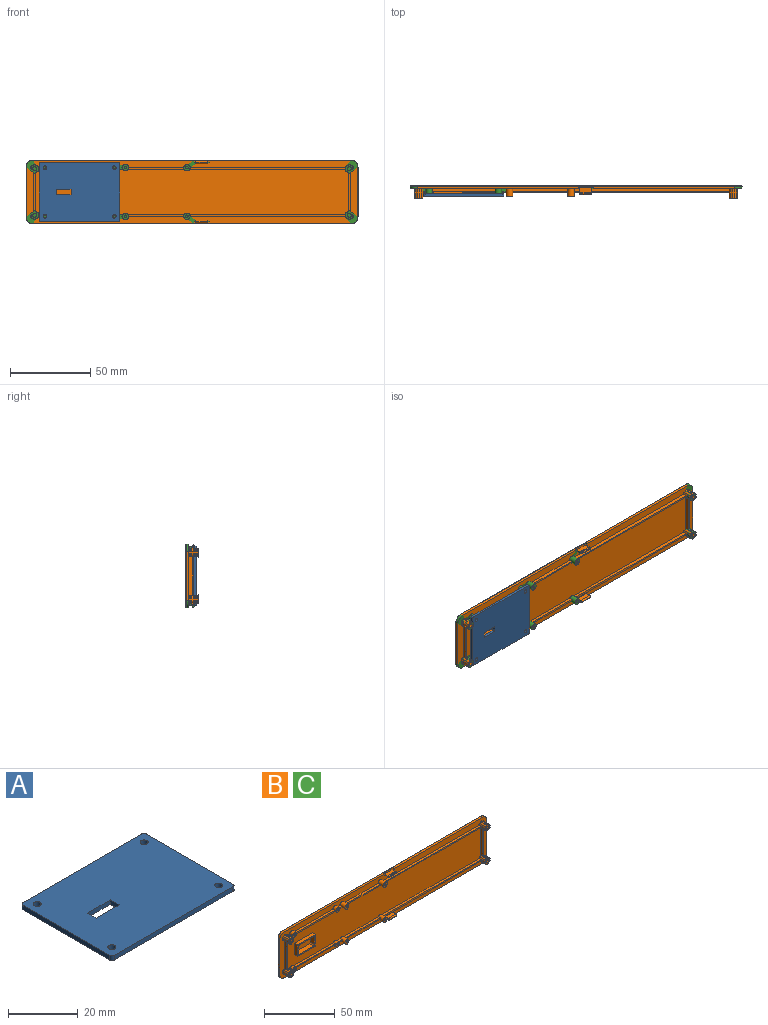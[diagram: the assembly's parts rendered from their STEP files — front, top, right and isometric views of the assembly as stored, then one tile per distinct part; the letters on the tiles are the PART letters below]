
ASSEMBLY  parts=3 mates=1
PART A: 18 faces, bbox 50x37x1.6 mm
  f0: cylinder r=1mm len=1.6mm, axis (0,0,-1), area 2.5mm2, adj f1,f15,f16,f17
  f1: plane 48x1.6mm, normal (0,-1,0), area 76.8mm2, adj f0,f2,f16,f17
  f2: cylinder r=1mm len=1.6mm, axis (0,0,-1), area 2.5mm2, adj f1,f3,f16,f17
  f3: plane 35x1.6mm, normal (1,0,0), area 56mm2, adj f2,f4,f16,f17
  f4: cylinder r=1mm len=1.6mm, axis (0,0,-1), area 2.5mm2, adj f3,f5,f16,f17
  f5: plane 48x1.6mm, normal (0,1,0), area 76.8mm2, adj f4,f6,f16,f17
  f6: cylinder r=1mm len=1.6mm, axis (0,0,-1), area 2.5mm2, adj f5,f15,f16,f17
  f7: plane 3.56x1.6mm, normal (-1,0,0), area 5.7mm2, adj f8,f14,f16,f17
  f8: plane 9.31x1.6mm, normal (0,1,0), area 14.9mm2, adj f7,f9,f16,f17
  f9: plane 3.56x1.6mm, normal (1,0,0), area 5.7mm2, adj f8,f14,f16,f17
  f10: cylinder r=1.15mm len=2.3mm, axis (0,0,-1), area 11.6mm2, adj f16,f17
  f11: cylinder r=1.15mm len=2.3mm, axis (0,0,-1), area 11.6mm2, adj f16,f17
  f12: cylinder r=1.15mm len=2.3mm, axis (0,0,-1), area 11.6mm2, adj f16,f17
  f13: cylinder r=1.15mm len=2.3mm, axis (0,0,-1), area 11.6mm2, adj f16,f17
  f14: plane 9.31x1.6mm, normal (0,-1,0), area 14.9mm2, adj f7,f9,f16,f17
  f15: plane 35x1.6mm, normal (-1,0,0), area 56mm2, adj f0,f6,f16,f17
  f16: plane 50x37mm, normal (0,0,1), area 1799.4mm2, adj f0,f1,f2,f3,f4,f5,f6,f7
  f17: plane 50x37mm, normal (0,0,-1), area 1799.4mm2, adj f0,f1,f2,f3,f4,f5,f6,f7
PART B: 227 faces, bbox 207.5x8x40.5 mm
  f0: cylinder r=0.3mm len=198mm, axis (-1,0,0), area 94.9mm2, adj f32,f36,f221,f222
  f1: cylinder r=0.3mm len=31mm, axis (0,0,-1), area 14.9mm2, adj f33,f36,f220,f222
  f2: cylinder r=0.3mm len=31mm, axis (0,0,1), area 14.9mm2, adj f34,f36,f219,f221
  f3: cylinder r=0.3mm len=198mm, axis (1,0,0), area 94.9mm2, adj f35,f36,f219,f220
  f4: cylinder r=1.25mm len=6mm, axis (0,-1,0), area 47.1mm2, adj f131,f150
  f5: cylinder r=2.7mm len=4mm, axis (0,-1,0), area 4mm2, adj f108,f110,f131,f204
  f6: cylinder r=1.25mm len=6mm, axis (0,-1,0), area 47.1mm2, adj f106,f127
  f7: cylinder r=2.7mm len=6mm, axis (0,-1,0), area 6mm2, adj f29,f106,f120,f121
  f8: cylinder r=1.25mm len=6mm, axis (0,-1,0), area 47.1mm2, adj f84,f102
  f9: cylinder r=2.7mm len=6mm, axis (0,-1,0), area 6mm2, adj f29,f84,f95,f96
  f10: cylinder r=1.25mm len=6mm, axis (0,-1,0), area 47.1mm2, adj f60,f80
  f11: cylinder r=2.7mm len=4mm, axis (0,-1,0), area 4mm2, adj f60,f73,f74,f200
  f12: cylinder r=0.8mm len=5mm, axis (0,-1,0), area 25.1mm2, adj f55,f56
  f13: cylinder r=0.8mm len=5mm, axis (0,-1,0), area 25.1mm2, adj f53,f54
  f14: cylinder r=0.8mm len=5mm, axis (0,-1,0), area 25.1mm2, adj f51,f52
  f15: cylinder r=0.8mm len=5mm, axis (0,-1,0), area 25.1mm2, adj f49,f50
  f16: cylinder r=2mm len=5mm, axis (0,-1,0), area 58.5mm2, adj f28,f29,f49,f211,f212,f213,f214,f215
  f17: cylinder r=0.8mm len=3mm, axis (0,1,0), area 15.1mm2, adj f47,f48
  f18: cylinder r=2mm len=4mm, axis (0,1,0), area 33.4mm2, adj f28,f29,f47,f208,f209,f210,f211,f212
  f19: cylinder r=0.8mm len=3mm, axis (0,1,0), area 15.1mm2, adj f45,f46
  f20: cylinder r=0.8mm len=3mm, axis (0,1,0), area 15.1mm2, adj f43,f44
  f21: cylinder r=0.8mm len=3mm, axis (0,1,0), area 15.1mm2, adj f41,f42
  f22: cylinder r=2mm len=4mm, axis (0,1,0), area 33.4mm2, adj f28,f29,f41,f205,f206,f207,f208,f209
  f23: cylinder r=2mm len=4mm, axis (0,1,0), area 33.4mm2, adj f28,f29,f43,f185,f186,f187,f188,f189
  f24: cylinder r=2mm len=5mm, axis (0,-1,0), area 58.6mm2, adj f28,f29,f53,f191,f192,f193,f194,f195
  f25: cylinder r=2mm len=4mm, axis (0,1,0), area 33.4mm2, adj f28,f29,f45,f188,f189,f190,f191,f192
  f26: cylinder r=2mm len=5mm, axis (0,-1,0), area 58.6mm2, adj f28,f29,f55,f194,f195,f196,f197,f198
  f27: cylinder r=2mm len=5mm, axis (0,-1,0), area 58.5mm2, adj f28,f29,f51,f201,f202,f203,f214,f215
  f28: plane 195x28mm, normal (0,-1,0), area 5253.7mm2, adj f16,f18,f22,f23,f24,f25,f26,f27
  f29: plane 206.7x39.7mm, normal (0,-1,0), area 2140.7mm2, adj f7,f9,f16,f18,f22,f23,f24,f25
  f30: cylinder r=2.3mm len=6mm, axis (0,-1,0), area 6.4mm2, adj f28,f29,f60,f68,f69,f201,f202,f203
  f31: cylinder r=2.3mm len=6mm, axis (0,-1,0), area 6.4mm2, adj f28,f29,f84,f90,f91,f197,f198,f199
  f32: plane 198x1.69mm, normal (0,-0.03,1), area 325.8mm2, adj f0,f29,f38,f40,f160,f161,f162
  f33: plane 31x1.69mm, normal (-1,-0.03,0), area 52.5mm2, adj f1,f29,f39,f40
  f34: plane 31x1.69mm, normal (1,-0.03,0), area 52.5mm2, adj f2,f29,f37,f38
  f35: plane 198x1.69mm, normal (0,-0.03,-1), area 325.8mm2, adj f3,f29,f37,f39,f172,f173,f174
  f36: plane 206.18x39.18mm, normal (0,1,0), area 8064.8mm2, adj f0,f1,f2,f3,f219,f220,f221,f222
  f37: cone r=4.4mm half-angle=1.5deg, axis (0,1,0), area 11.6mm2, adj f29,f34,f35,f219
  f38: cone r=4.4mm half-angle=1.5deg, axis (0,1,0), area 11.6mm2, adj f29,f32,f34,f221
  f39: cone r=4.4mm half-angle=1.5deg, axis (0,1,0), area 11.6mm2, adj f29,f33,f35,f220
  f40: cone r=4.4mm half-angle=1.5deg, axis (0,1,0), area 11.6mm2, adj f29,f32,f33,f222
  f41: plane 4x4mm, normal (0,-1,0), area 10.6mm2, adj f21,f22
  f42: plane 1.6x1.6mm, normal (0,-1,0), area 2mm2, adj f21
  f43: plane 4x4mm, normal (0,-1,0), area 10.6mm2, adj f20,f23
  f44: plane 1.6x1.6mm, normal (0,-1,0), area 2mm2, adj f20
  f45: plane 4x4mm, normal (0,-1,0), area 10.6mm2, adj f19,f25
  f46: plane 1.6x1.6mm, normal (0,-1,0), area 2mm2, adj f19
  f47: plane 4x4mm, normal (0,-1,0), area 10.6mm2, adj f17,f18
  f48: plane 1.6x1.6mm, normal (0,-1,0), area 2mm2, adj f17
  f49: plane 4x4mm, normal (0,-1,0), area 10.6mm2, adj f15,f16
  f50: plane 1.6x1.6mm, normal (0,-1,0), area 2mm2, adj f15
  f51: plane 4x4mm, normal (0,-1,0), area 10.6mm2, adj f14,f27
  f52: plane 1.6x1.6mm, normal (0,-1,0), area 2mm2, adj f14
  f53: plane 4x4mm, normal (0,-1,0), area 10.6mm2, adj f13,f24
  f54: plane 1.6x1.6mm, normal (0,-1,0), area 2mm2, adj f13
  f55: plane 4x4mm, normal (0,-1,0), area 10.6mm2, adj f12,f26
  f56: plane 1.6x1.6mm, normal (0,-1,0), area 2mm2, adj f12
  f57: cylinder r=2.7mm len=6mm, axis (0,-1,0), area 6mm2, adj f29,f58,f59,f60
  f58: plane 6x0.35mm, normal (0.5,0,-0.87), area 2.4mm2, adj f29,f57,f60,f79
  f59: plane 6x0.35mm, normal (-0.5,0,0.87), area 2.4mm2, adj f29,f57,f60,f61
  f60: plane 5.4x5.1mm, normal (0,-1,0), area 14.1mm2, adj f10,f11,f30,f57,f58,f59,f61,f62
  f61: cylinder r=2.3mm len=6mm, axis (0,-1,0), area 8.4mm2, adj f29,f59,f60,f62
  f62: plane 6x0.41mm, normal (1,0,0), area 2.4mm2, adj f29,f60,f61,f63
  f63: cylinder r=2.7mm len=6mm, axis (0,-1,0), area 6mm2, adj f29,f60,f62,f64
  f64: plane 6x0.41mm, normal (-1,0,0), area 2.4mm2, adj f29,f60,f63,f65
  f65: cylinder r=2.3mm len=6mm, axis (0,-1,0), area 8.4mm2, adj f29,f60,f64,f66
  f66: plane 6x0.35mm, normal (0.5,0,0.87), area 2.4mm2, adj f29,f60,f65,f67
  f67: cylinder r=2.7mm len=6mm, axis (0,-1,0), area 6mm2, adj f29,f60,f66,f68
  f68: plane 6x0.35mm, normal (-0.5,0,-0.87), area 2.4mm2, adj f29,f30,f60,f67
  f69: plane 6x0.35mm, normal (-0.5,0,0.87), area 2.4mm2, adj f28,f30,f60,f70
  f70: cylinder r=2.7mm len=6mm, axis (0,-1,0), area 6mm2, adj f28,f60,f69,f71
  f71: plane 6x0.35mm, normal (0.5,0,-0.87), area 2.4mm2, adj f28,f60,f70,f72
  f72: cylinder r=2.3mm len=6mm, axis (0,-1,0), area 8.4mm2, adj f28,f60,f71,f73
  f73: plane 24.51x6mm, normal (-1,0,0), area 52.3mm2, adj f11,f28,f60,f72,f84,f86,f87,f200
  f74: plane 24.51x6mm, normal (1,0,0), area 52.3mm2, adj f11,f29,f60,f75,f84,f85,f86,f200
  f75: cylinder r=2.3mm len=6mm, axis (0,-1,0), area 8.4mm2, adj f29,f60,f74,f76
  f76: plane 6x0.35mm, normal (-0.5,0,-0.87), area 2.4mm2, adj f29,f60,f75,f77
  f77: cylinder r=2.7mm len=6mm, axis (0,-1,0), area 6mm2, adj f29,f60,f76,f78
  f78: plane 6x0.35mm, normal (0.5,0,0.87), area 2.4mm2, adj f29,f60,f77,f79
  f79: cylinder r=2.3mm len=6mm, axis (0,-1,0), area 8.4mm2, adj f29,f58,f60,f78
  f80: plane 2.5x2.5mm, normal (0,-1,0), area 4.9mm2, adj f10
  f81: cylinder r=2.7mm len=6mm, axis (0,-1,0), area 6mm2, adj f29,f82,f83,f84
  f82: plane 6x0.35mm, normal (0.5,0,-0.87), area 2.4mm2, adj f29,f81,f84,f101
  f83: plane 6x0.35mm, normal (-0.5,0,0.87), area 2.4mm2, adj f29,f81,f84,f85
  f84: plane 5.4x5.1mm, normal (0,-1,0), area 14.1mm2, adj f8,f9,f31,f73,f74,f81,f82,f83
  f85: cylinder r=2.3mm len=6mm, axis (0,-1,0), area 8.4mm2, adj f29,f74,f83,f84
  f86: cylinder r=2.7mm len=4mm, axis (0,-1,0), area 4mm2, adj f73,f74,f84,f200
  f87: cylinder r=2.3mm len=6mm, axis (0,-1,0), area 8.4mm2, adj f28,f73,f84,f88
  f88: plane 6x0.35mm, normal (0.5,0,0.87), area 2.4mm2, adj f28,f84,f87,f89
  f89: cylinder r=2.7mm len=6mm, axis (0,-1,0), area 6mm2, adj f28,f84,f88,f90
  f90: plane 6x0.35mm, normal (-0.5,0,-0.87), area 2.4mm2, adj f28,f31,f84,f89
  f91: plane 6x0.35mm, normal (-0.5,0,0.87), area 2.4mm2, adj f29,f31,f84,f92
  f92: cylinder r=2.7mm len=6mm, axis (0,-1,0), area 6mm2, adj f29,f84,f91,f93
  f93: plane 6x0.35mm, normal (0.5,0,-0.87), area 2.4mm2, adj f29,f84,f92,f94
  f94: cylinder r=2.3mm len=6mm, axis (0,-1,0), area 8.4mm2, adj f29,f84,f93,f95
  f95: plane 6x0.41mm, normal (-1,0,0), area 2.4mm2, adj f9,f29,f84,f94
  f96: plane 6x0.41mm, normal (1,0,0), area 2.4mm2, adj f9,f29,f84,f97
  f97: cylinder r=2.3mm len=6mm, axis (0,-1,0), area 8.4mm2, adj f29,f84,f96,f98
  f98: plane 6x0.35mm, normal (-0.5,0,-0.87), area 2.4mm2, adj f29,f84,f97,f99
  f99: cylinder r=2.7mm len=6mm, axis (0,-1,0), area 6mm2, adj f29,f84,f98,f100
  f100: plane 6x0.35mm, normal (0.5,0,0.87), area 2.4mm2, adj f29,f84,f99,f101
  f101: cylinder r=2.3mm len=6mm, axis (0,-1,0), area 8.4mm2, adj f29,f82,f84,f100
  f102: plane 2.5x2.5mm, normal (0,-1,0), area 4.9mm2, adj f8
  f103: cylinder r=2.7mm len=6mm, axis (0,-1,0), area 6mm2, adj f28,f104,f105,f106
  f104: plane 6x0.35mm, normal (0.5,0,-0.87), area 2.4mm2, adj f28,f103,f106,f126
  f105: plane 6x0.35mm, normal (-0.5,0,0.87), area 2.4mm2, adj f28,f103,f106,f107
  f106: plane 5.4x5.1mm, normal (0,-1,0), area 14.1mm2, adj f6,f7,f103,f104,f105,f107,f108,f109
  f107: cylinder r=2.3mm len=6mm, axis (0,-1,0), area 8.4mm2, adj f28,f105,f106,f108
  f108: plane 24.51x6mm, normal (1,0,0), area 52.3mm2, adj f5,f28,f106,f107,f109,f131,f145,f204
  f109: cylinder r=2.7mm len=4mm, axis (0,-1,0), area 4mm2, adj f106,f108,f110,f204
  f110: plane 24.51x6mm, normal (-1,0,0), area 52.3mm2, adj f5,f29,f106,f109,f111,f131,f144,f204
  f111: cylinder r=2.3mm len=6mm, axis (0,-1,0), area 8.4mm2, adj f29,f106,f110,f112
  f112: plane 6x0.35mm, normal (0.5,0,0.87), area 2.4mm2, adj f29,f106,f111,f113
  f113: cylinder r=2.7mm len=6mm, axis (0,-1,0), area 6mm2, adj f29,f106,f112,f114
  f114: plane 6x0.35mm, normal (-0.5,0,-0.87), area 2.4mm2, adj f29,f106,f113,f115
  f115: cylinder r=2.3mm len=6mm, axis (0,-1,0), area 8.4mm2, adj f29,f106,f114,f116
  f116: plane 6x0.35mm, normal (-0.5,0,0.87), area 2.4mm2, adj f29,f106,f115,f117
  f117: cylinder r=2.7mm len=6mm, axis (0,-1,0), area 6mm2, adj f29,f106,f116,f118
  f118: plane 6x0.35mm, normal (0.5,0,-0.87), area 2.4mm2, adj f29,f106,f117,f119
  f119: cylinder r=2.3mm len=6mm, axis (0,-1,0), area 8.4mm2, adj f29,f106,f118,f120
  f120: plane 6x0.41mm, normal (-1,0,0), area 2.4mm2, adj f7,f29,f106,f119
  f121: plane 6x0.41mm, normal (1,0,0), area 2.4mm2, adj f7,f29,f106,f122
  f122: cylinder r=2.3mm len=6mm, axis (0,-1,0), area 8.4mm2, adj f29,f106,f121,f123
  f123: plane 6x0.35mm, normal (-0.5,0,-0.87), area 2.4mm2, adj f29,f106,f122,f124
  f124: cylinder r=2.7mm len=6mm, axis (0,-1,0), area 6mm2, adj f29,f106,f123,f125
  f125: plane 6x0.35mm, normal (0.5,0,0.87), area 2.4mm2, adj f29,f106,f124,f126
  f126: cylinder r=2.3mm len=6mm, axis (0,-1,0), area 6.4mm2, adj f28,f29,f104,f106,f125,f185,f186,f187
  f127: plane 2.5x2.5mm, normal (0,-1,0), area 4.9mm2, adj f6
  f128: cylinder r=2.7mm len=6mm, axis (0,-1,0), area 6mm2, adj f29,f129,f130,f131
  f129: plane 6x0.35mm, normal (0.5,0,-0.87), area 2.4mm2, adj f29,f128,f131,f149
  f130: plane 6x0.35mm, normal (-0.5,0,0.87), area 2.4mm2, adj f29,f128,f131,f132
  f131: plane 5.4x5.1mm, normal (0,-1,0), area 14.1mm2, adj f4,f5,f108,f110,f128,f129,f130,f132
  f132: cylinder r=2.3mm len=6mm, axis (0,-1,0), area 8.4mm2, adj f29,f130,f131,f133
  f133: plane 6x0.41mm, normal (1,0,0), area 2.4mm2, adj f29,f131,f132,f134
  f134: cylinder r=2.7mm len=6mm, axis (0,-1,0), area 6mm2, adj f29,f131,f133,f135
  f135: plane 6x0.41mm, normal (-1,0,0), area 2.4mm2, adj f29,f131,f134,f136
  f136: cylinder r=2.3mm len=6mm, axis (0,-1,0), area 8.4mm2, adj f29,f131,f135,f137
  f137: plane 6x0.35mm, normal (0.5,0,0.87), area 2.4mm2, adj f29,f131,f136,f138
  f138: cylinder r=2.7mm len=6mm, axis (0,-1,0), area 6mm2, adj f29,f131,f137,f139
  f139: plane 6x0.35mm, normal (-0.5,0,-0.87), area 2.4mm2, adj f29,f131,f138,f140
  f140: cylinder r=2.3mm len=6mm, axis (0,-1,0), area 8.4mm2, adj f29,f131,f139,f141
  f141: plane 6x0.35mm, normal (-0.5,0,0.87), area 2.4mm2, adj f29,f131,f140,f142
  f142: cylinder r=2.7mm len=6mm, axis (0,-1,0), area 6mm2, adj f29,f131,f141,f143
  f143: plane 6x0.35mm, normal (0.5,0,-0.87), area 2.4mm2, adj f29,f131,f142,f144
  f144: cylinder r=2.3mm len=6mm, axis (0,-1,0), area 8.4mm2, adj f29,f110,f131,f143
  f145: cylinder r=2.3mm len=6mm, axis (0,-1,0), area 8.4mm2, adj f28,f108,f131,f146
  f146: plane 6x0.35mm, normal (-0.5,0,-0.87), area 2.4mm2, adj f28,f131,f145,f147
  f147: cylinder r=2.7mm len=6mm, axis (0,-1,0), area 6mm2, adj f28,f131,f146,f148
  f148: plane 6x0.35mm, normal (0.5,0,0.87), area 2.4mm2, adj f28,f131,f147,f149
  f149: cylinder r=2.3mm len=6mm, axis (0,-1,0), area 6.4mm2, adj f28,f29,f129,f131,f148,f205,f206,f207
  f150: plane 2.5x2.5mm, normal (0,-1,0), area 4.9mm2, adj f4
  f151: plane 3.79x1.77mm, normal (-1,0,0), area 4.2mm2, adj f29,f152,f154,f155,f156,f157,f158,f159
  f152: plane 9.4x3.6mm, normal (0,0,1), area 28.6mm2, adj f29,f151,f153,f155,f160,f161,f162
  f153: plane 3.79x1.77mm, normal (1,0,0), area 4.2mm2, adj f29,f152,f154,f155,f156,f157,f158,f159
  f154: plane 7.4x2.8mm, normal (0,0,-1), area 20.7mm2, adj f29,f151,f153,f159
  f155: plane 7.4x0.47mm, normal (0,1,0), area 3.5mm2, adj f151,f152,f153,f217
  f156: plane 7.4x0.11mm, normal (0,-0.71,0.71), area 1.2mm2, adj f151,f153,f157,f158
  f157: cylinder r=1mm len=7.4mm, axis (1,0,0), area 3.5mm2, adj f151,f153,f156,f217
  f158: cylinder r=1mm len=7.4mm, axis (-1,0,0), area 4.6mm2, adj f151,f153,f156,f159
  f159: cylinder r=1mm len=7.4mm, axis (-1,0,0), area 10.5mm2, adj f151,f153,f154,f158
  f160: plane 9.4x1.22mm, normal (0,-1,0), area 11.5mm2, adj f32,f152,f161,f162
  f161: plane 1.22x1mm, normal (1,0,0), area 1.2mm2, adj f29,f32,f152,f160
  f162: plane 1.22x1mm, normal (-1,0,0), area 1.2mm2, adj f29,f32,f152,f160
  f163: plane 9.4x3.5mm, normal (0,0,-1), area 27.9mm2, adj f29,f164,f166,f167,f172,f173,f174
  f164: plane 3.79x1.79mm, normal (1,0,0), area 4.3mm2, adj f29,f163,f165,f167,f168,f169,f170,f171
  f165: plane 7.4x2.8mm, normal (0,0,1), area 20.7mm2, adj f29,f164,f166,f171
  f166: plane 3.79x1.79mm, normal (-1,0,0), area 4.3mm2, adj f29,f163,f165,f167,f168,f169,f170,f171
  f167: plane 7.4x0.49mm, normal (0,1,0), area 3.6mm2, adj f163,f164,f166,f218
  f168: plane 7.4x0.11mm, normal (0,-0.71,-0.71), area 1.2mm2, adj f164,f166,f169,f170
  f169: cylinder r=1mm len=7.4mm, axis (-1,0,0), area 4.6mm2, adj f164,f166,f168,f218
  f170: cylinder r=1mm len=7.4mm, axis (-1,0,0), area 4.6mm2, adj f164,f166,f168,f171
  f171: cylinder r=1mm len=7.4mm, axis (1,0,0), area 10.5mm2, adj f164,f165,f166,f170
  f172: plane 9.4x1.22mm, normal (0,-1,0), area 11.5mm2, adj f35,f163,f173,f174
  f173: plane 1.22x1mm, normal (1,0,0), area 1.2mm2, adj f29,f35,f163,f172
  f174: plane 1.22x1mm, normal (-1,0,0), area 1.2mm2, adj f29,f35,f163,f172
  f175: plane 18x3mm, normal (0,0,1), area 54mm2, adj f28,f176,f178,f179
  f176: plane 10x3mm, normal (-1,0,0), area 30mm2, adj f28,f175,f177,f179
  f177: plane 18x3mm, normal (0,0,-1), area 54mm2, adj f28,f176,f178,f179
  f178: plane 10x3mm, normal (1,0,0), area 30mm2, adj f28,f175,f177,f179
  f179: plane 18x10mm, normal (0,-1,0), area 52.9mm2, adj f175,f176,f177,f178,f180,f181,f182,f183
  f180: plane 6x4mm, normal (1,0,0), area 24mm2, adj f179,f184,f225,f226
  f181: plane 14x4mm, normal (0,0,1), area 56mm2, adj f179,f184,f223,f226
  f182: plane 6x4mm, normal (-1,0,0), area 24mm2, adj f179,f184,f223,f224
  f183: plane 14x4mm, normal (0,0,-1), area 56mm2, adj f179,f184,f224,f225
  f184: plane 16x8mm, normal (0,-1,0), area 127.1mm2, adj f180,f181,f182,f183,f223,f224,f225,f226
  f185: plane 2.48x2mm, normal (0,0,1), area 4.9mm2, adj f23,f28,f126,f187
  f186: plane 2.13x2mm, normal (0,0,-1), area 4.3mm2, adj f23,f29,f126,f187
  f187: plane 2.48x1mm, normal (0,-1,0), area 2.2mm2, adj f23,f126,f185,f186
  f188: plane 39.27x2mm, normal (0,0,-1), area 78.5mm2, adj f23,f25,f29,f190
  f189: plane 39.96x2mm, normal (0,0,1), area 79.9mm2, adj f23,f25,f28,f190
  f190: plane 39.96x1mm, normal (0,-1,0), area 39.5mm2, adj f23,f25,f188,f189
  f191: plane 2.94x2mm, normal (0,0,-1), area 5.9mm2, adj f24,f25,f29,f193
  f192: plane 3.63x2mm, normal (0,0,1), area 7.3mm2, adj f24,f25,f28,f193
  f193: plane 3.63x1mm, normal (0,-1,0), area 3.2mm2, adj f24,f25,f191,f192
  f194: plane 34.94x2mm, normal (0,0,1), area 69.9mm2, adj f24,f26,f28,f196
  f195: plane 34.26x2mm, normal (0,0,-1), area 68.5mm2, adj f24,f26,f29,f196
  f196: plane 34.94x1mm, normal (0,-1,0), area 34.5mm2, adj f24,f26,f194,f195
  f197: plane 96.94x2mm, normal (0,0,-1), area 193.9mm2, adj f26,f29,f31,f199
  f198: plane 97.28x2mm, normal (0,0,1), area 194.6mm2, adj f26,f28,f31,f199
  f199: plane 97.28x1mm, normal (0,-1,0), area 97mm2, adj f26,f31,f197,f198
  f200: plane 23.69x1mm, normal (0,-1,0), area 23.6mm2, adj f11,f73,f74,f86
  f201: plane 97.29x2mm, normal (0,0,-1), area 194.6mm2, adj f27,f28,f30,f203
  f202: plane 96.94x2mm, normal (0,0,1), area 193.9mm2, adj f27,f29,f30,f203
  f203: plane 97.29x1mm, normal (0,-1,0), area 97mm2, adj f27,f30,f201,f202
  f204: plane 23.69x1mm, normal (0,-1,0), area 23.6mm2, adj f5,f108,f109,f110
  f205: plane 2.13x2mm, normal (0,0,1), area 4.3mm2, adj f22,f29,f149,f207
  f206: plane 2.48x2mm, normal (0,0,-1), area 4.9mm2, adj f22,f28,f149,f207
  f207: plane 2.48x1mm, normal (0,-1,0), area 2.2mm2, adj f22,f149,f205,f206
  f208: plane 39.27x2mm, normal (0,0,1), area 78.5mm2, adj f18,f22,f29,f210
  f209: plane 39.96x2mm, normal (0,0,-1), area 79.9mm2, adj f18,f22,f28,f210
  f210: plane 39.96x1mm, normal (0,-1,0), area 39.5mm2, adj f18,f22,f208,f209
  f211: plane 2.94x2mm, normal (0,0,1), area 5.9mm2, adj f16,f18,f29,f213
  f212: plane 3.64x2mm, normal (0,0,-1), area 7.3mm2, adj f16,f18,f28,f213
  f213: plane 3.64x1mm, normal (0,-1,0), area 3.2mm2, adj f16,f18,f211,f212
  f214: plane 34.27x2mm, normal (0,0,1), area 68.5mm2, adj f16,f27,f29,f216
  f215: plane 34.96x2mm, normal (0,0,-1), area 69.9mm2, adj f16,f27,f28,f216
  f216: plane 34.96x1mm, normal (0,-1,0), area 34.5mm2, adj f16,f27,f214,f215
  f217: cylinder r=0.3mm len=7.4mm, axis (1,0,0), area 4.2mm2, adj f151,f153,f155,f157
  f218: cylinder r=0.3mm len=7.4mm, axis (-1,0,0), area 3.9mm2, adj f164,f166,f167,f169
  f219: torus R=4.09mm, axis (0,-1,0), area 3.2mm2, adj f2,f3,f36,f37
  f220: torus R=4.09mm, axis (0,-1,0), area 3.2mm2, adj f1,f3,f36,f39
  f221: torus R=4.09mm, axis (0,-1,0), area 3.2mm2, adj f0,f2,f36,f38
  f222: torus R=4.09mm, axis (0,-1,0), area 3.2mm2, adj f0,f1,f36,f40
  f223: cylinder r=1mm len=4mm, axis (0,-1,0), area 6.3mm2, adj f179,f181,f182,f184
  f224: cylinder r=1mm len=4mm, axis (0,-1,0), area 6.3mm2, adj f179,f182,f183,f184
  f225: cylinder r=1mm len=4mm, axis (0,-1,0), area 6.3mm2, adj f179,f180,f183,f184
  f226: cylinder r=1mm len=4mm, axis (0,-1,0), area 6.3mm2, adj f179,f180,f181,f184
PART C: same geometry as B
PLACE A rot(axis=(-1,0,0),90deg) t=(9.35,1.78,-107.41)mm
PLACE B t=(5.18,-18.62,2.09)mm fixed
PLACE C t=(5.18,-18.62,2.09)mm
MATE fastened A.f10 <-> B.f17  axis (0,1,0) through (-43.19,3.38,17.22)mm
